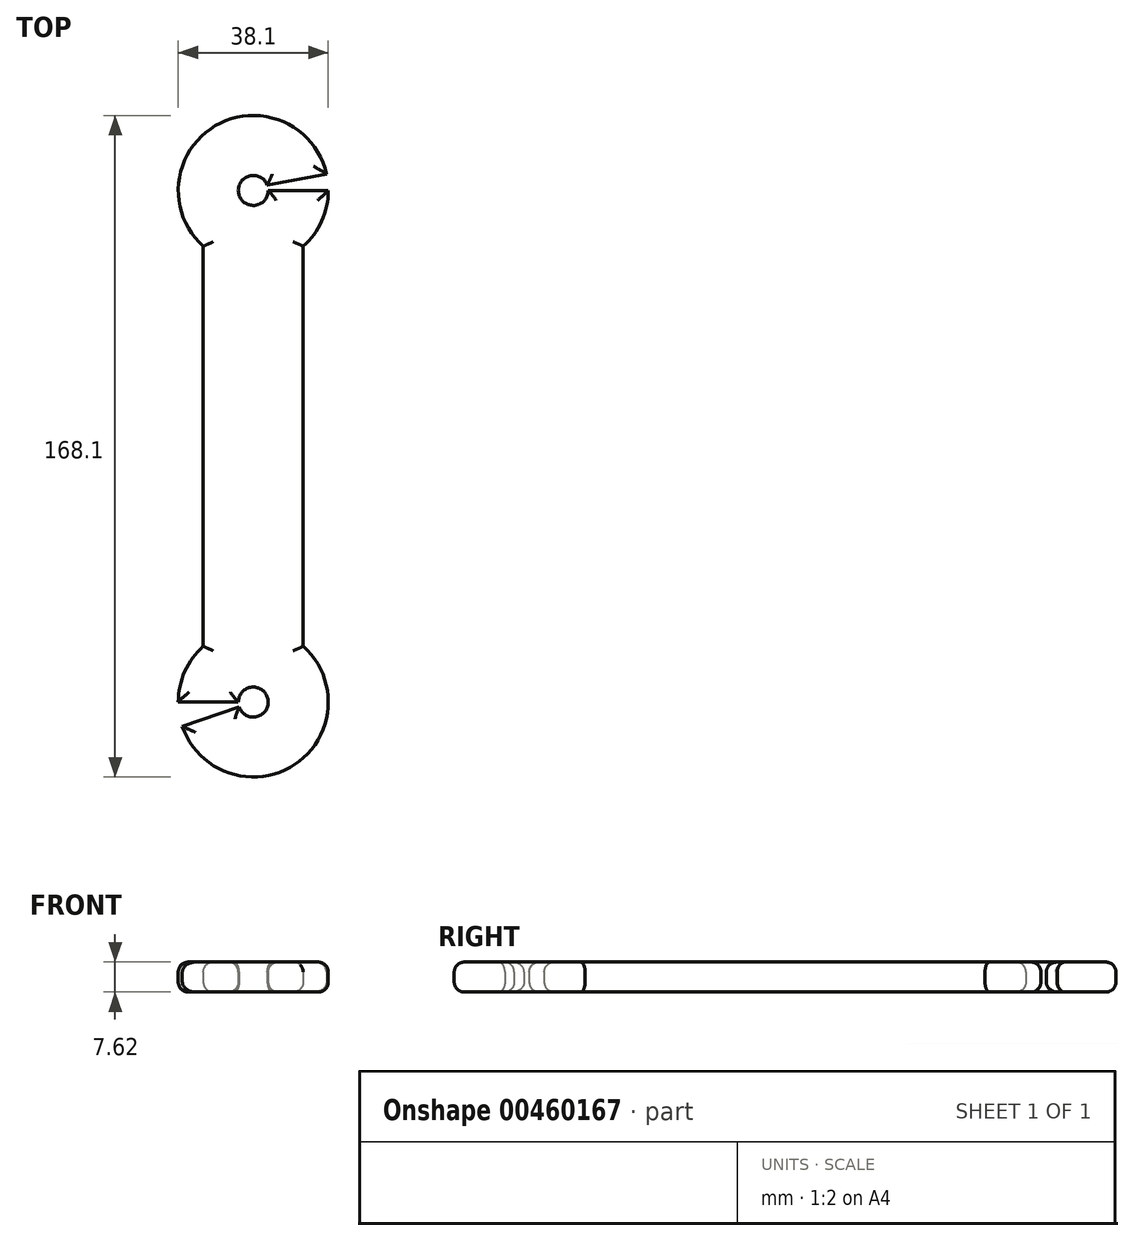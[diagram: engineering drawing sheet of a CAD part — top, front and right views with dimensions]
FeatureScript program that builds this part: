
annotation { "Feature Type Name" : "Feature", "Feature Type Description" : "" }
export const myFeature = defineFeature(function(context is Context, id is Id, definition is map)
    precondition{}
    {
        {
            var Q0;
            Q0=qCreatedBy(makeId("Top.planeOp"),FACE);
            var sketch = newSketch(context, id + "F0", { "sketchPlane" : qUnion([Q0])});
            skArc(sketch, "E0", {"start": v(-20.06, 50.8) * mm, "mid": v(-15.37, 57.22) * mm, "end": v(-13.71, 65) * mm});
            skArc(sketch, "E1.MirrorC", {"start": v(-20.06, -50.8) * mm, "mid": v(-22.23, -80.87) * mm, "end": v(-50.78, -71.18) * mm});
            skLineSegment(sketch, "E2", {"start": v(-20.06, 50.8) * mm, "end": v(-20.06, -50.8) * mm});
            skArc(sketch, "E3", {"start": v(-36.36, -66.27) * mm, "mid": v(-29, -64.35) * mm, "end": v(-36.57, -65) * mm});
            skArc(sketch, "E4", {"start": v(-29.2, 66.36) * mm, "mid": v(-36.5, 64.3) * mm, "end": v(-28.95, 65) * mm});
            skLineSegment(sketch, "E5.MirrorCS", {"start": v(-45.46, 50.8) * mm, "end": v(-45.46, -50.8) * mm});
            skLineSegment(sketch, "E6", {"start": v(-36.57, -65) * mm, "end": v(-51.81, -65) * mm});
            skLineSegment(sketch, "E7", {"start": v(-36.36, -66.27) * mm, "end": v(-50.78, -71.18) * mm});
            skArc(sketch, "E8.trimOffspring", {"start": v(-51.81, -65) * mm, "mid": v(-50.15, -57.22) * mm, "end": v(-45.46, -50.8) * mm});
            skLineSegment(sketch, "E9", {"start": v(-28.95, 65) * mm, "end": v(-13.71, 65) * mm});
            skLineSegment(sketch, "E10", {"start": v(-29.18, 66.37) * mm, "end": v(-14.17, 69.16) * mm});
            skArc(sketch, "E11.trimOffspring", {"start": v(-14.17, 69.16) * mm, "mid": v(-42.4, 81.43) * mm, "end": v(-45.46, 50.8) * mm});
            skLineSegment(sketch, "E12", {"start": v(-29.18, 66.37) * mm, "end": v(-29.2, 66.36) * mm});
            skSolve(sketch);
        }
        {
            var Q0;
            Q0=makeQuery(id+"F0.imprint","IMPRINT",FACE,{"disambiguationData":[TD([[makeQuery(id+"F0.imprint","IMPRINT",EDGE,{"derivedFrom":sQuery(id+"F0.wireOp",EDGE,"E0")}),1.0]])]});
            extrude(context, id + "F1", {"entities" : qUnion([Q0]), "depth" : 7.62 * mm});
        }
        {
            var Q0;
            Q0=makeQuery(id+"F1.opExtrude","CAP_EDGE",EDGE,{"disambiguationData":[OSD([sQuery(id+"F0.wireOp",EDGE,"E1.MirrorC")])],"isStart":false});
            var Q1;
            Q1=makeQuery(id+"F1.opExtrude","CAP_EDGE",EDGE,{"disambiguationData":[OSD([sQuery(id+"F0.wireOp",EDGE,"E2")])],"isStart":false});
            var Q2;
            Q2=makeQuery(id+"F1.opExtrude","CAP_FACE",FACE,{"disambiguationData":[OSD([sQuery(id+"F0.wireOp",EDGE,"E0"),sQuery(id+"F0.wireOp",EDGE,"E1.MirrorC"),sQuery(id+"F0.wireOp",EDGE,"E2"),sQuery(id+"F0.wireOp",EDGE,"E3"),sQuery(id+"F0.wireOp",EDGE,"E4"),sQuery(id+"F0.wireOp",EDGE,"E5.MirrorCS"),sQuery(id+"F0.wireOp",EDGE,"E6"),sQuery(id+"F0.wireOp",EDGE,"E7"),sQuery(id+"F0.wireOp",EDGE,"E8.trimOffspring"),sQuery(id+"F0.wireOp",EDGE,"E9"),sQuery(id+"F0.wireOp",EDGE,"E10"),sQuery(id+"F0.wireOp",EDGE,"E11.trimOffspring"),sQuery(id+"F0.wireOp",EDGE,"E12")])],"isStart":false});
            fillet(context, id + "F2", {"entities" : qUnion([Q0, Q1, Q2]), "radius" : 2.54 * mm, "tangentPropagation" : true, "allowEdgeOverflow" : false});
        }
        {
            var Q0;
            Q0=makeQuery(id+"F1.opExtrude","CAP_FACE",FACE,{"disambiguationData":[OSD([sQuery(id+"F0.wireOp",EDGE,"E0"),sQuery(id+"F0.wireOp",EDGE,"E1.MirrorC"),sQuery(id+"F0.wireOp",EDGE,"E2"),sQuery(id+"F0.wireOp",EDGE,"E3"),sQuery(id+"F0.wireOp",EDGE,"E4"),sQuery(id+"F0.wireOp",EDGE,"E5.MirrorCS"),sQuery(id+"F0.wireOp",EDGE,"E6"),sQuery(id+"F0.wireOp",EDGE,"E7"),sQuery(id+"F0.wireOp",EDGE,"E8.trimOffspring"),sQuery(id+"F0.wireOp",EDGE,"E9"),sQuery(id+"F0.wireOp",EDGE,"E10"),sQuery(id+"F0.wireOp",EDGE,"E11.trimOffspring"),sQuery(id+"F0.wireOp",EDGE,"E12")])],"isStart":true});
            fillet(context, id + "F3", {"entities" : qUnion([Q0]), "radius" : 2.54 * mm, "tangentPropagation" : true, "allowEdgeOverflow" : false});
        }
    });
